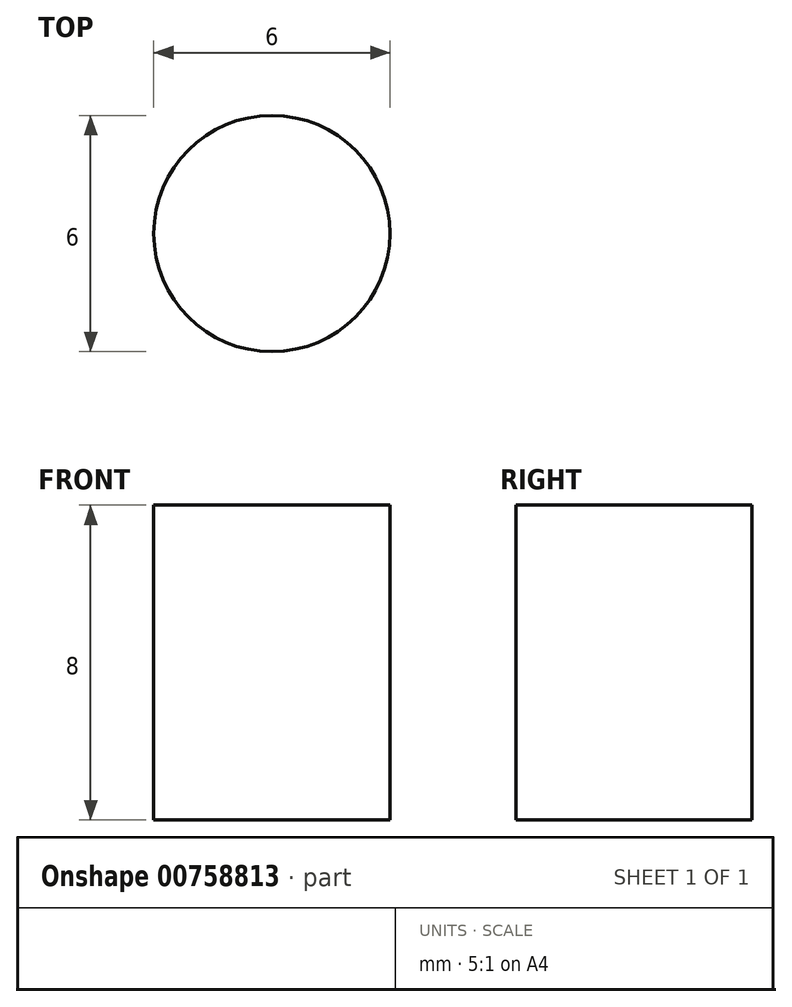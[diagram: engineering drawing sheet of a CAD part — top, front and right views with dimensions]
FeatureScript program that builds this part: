
annotation { "Feature Type Name" : "Feature", "Feature Type Description" : "" }
export const myFeature = defineFeature(function(context is Context, id is Id, definition is map)
    precondition{}
    {
        {
            var Q0;
            Q0=qCreatedBy(makeId("Front.planeOp"),FACE);
            var sketch = newSketch(context, id + "F0", { "sketchPlane" : qUnion([Q0])});
            skLineSegment(sketch, "E0.bottom", {"start": v(0, 0) * mm, "end": v(3, 0) * mm});
            skLineSegment(sketch, "E0.top", {"start": v(0, 8) * mm, "end": v(3, 8) * mm});
            skLineSegment(sketch, "E0.left", {"start": v(0, 0) * mm, "end": v(0, 8) * mm});
            skLineSegment(sketch, "E0.right", {"start": v(3, 0) * mm, "end": v(3, 8) * mm});
            skLineSegment(sketch, "E1", {"start": v(0, 0) * mm, "end": v(0, 14.3) * mm, "construction": true});
            skSolve(sketch);
        }
        {
            var Q0;
            Q0=makeQuery(id+"F0.imprint","IMPRINT",FACE,{"disambiguationData":[TD([[makeQuery(id+"F0.imprint","IMPRINT",EDGE,{"derivedFrom":sQuery(id+"F0.wireOp",EDGE,"E0.bottom")}),1.0]])]});
            var Q1;
            Q1=sQuery(id+"F0.wireOp",EDGE,"E1");
            revolve(context, id + "F1", {"surfaceOperationType" : NewSurfaceOperationType.NEW, "entities" : qUnion([Q0]), "axis" : qUnion([Q1]), "revolveType" : RevolveType.ONE_DIRECTION, "angle" : 360 * degree});
        }
    });
